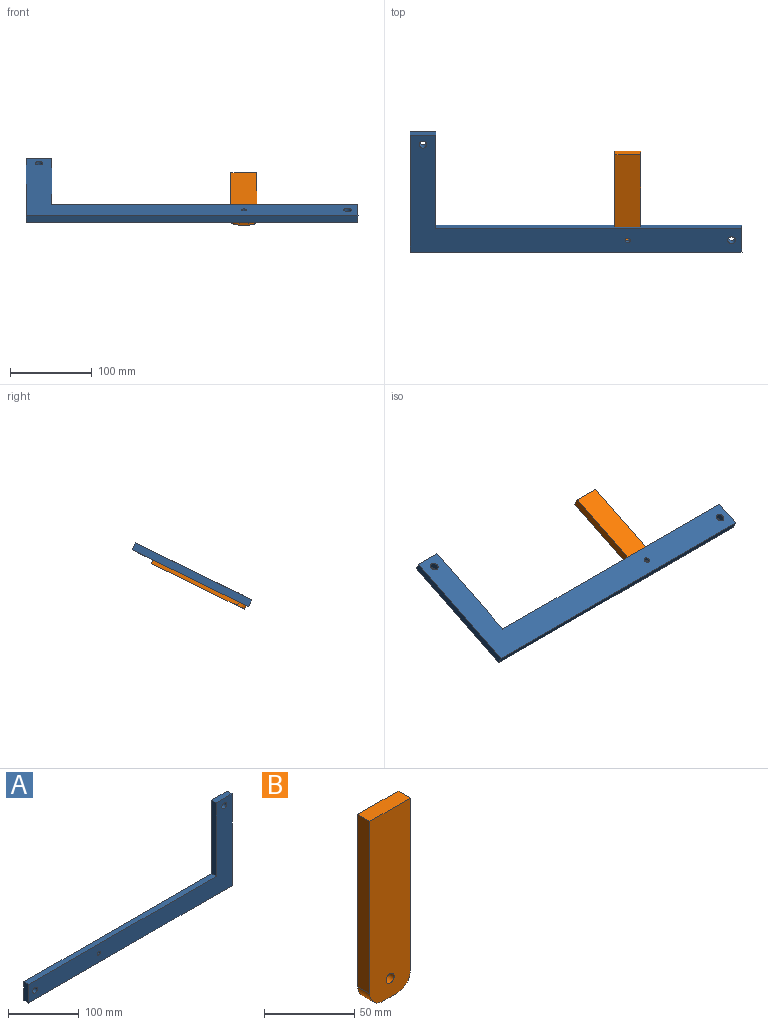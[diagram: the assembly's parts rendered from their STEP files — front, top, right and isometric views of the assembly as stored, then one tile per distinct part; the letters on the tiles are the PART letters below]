
ASSEMBLY  parts=2 mates=1
PART A: 11 faces, bbox 406.4x9.5x158.8 mm
  f0: plane 406.4x9.53mm, normal (0,0,-1), area 3871mm2, adj f1,f7,f9,f10
  f1: plane 158.75x9.53mm, normal (1,0,0), area 1512.1mm2, adj f0,f2,f9,f10
  f2: plane 31.75x9.53mm, normal (0,0,1), area 302.4mm2, adj f1,f3,f9,f10
  f3: plane 127x9.53mm, normal (-1,0,0), area 1209.7mm2, adj f2,f4,f9,f10
  f4: plane 374.65x9.53mm, normal (0,0,1), area 3568.5mm2, adj f3,f7,f9,f10
  f5: cylinder r=3.17mm len=9.53mm, axis (0,1,0), area 190mm2, adj f9,f10
  f6: cylinder r=4.76mm len=9.53mm, axis (0,1,0), area 285mm2, adj f9,f10
  f7: plane 31.75x9.53mm, normal (-1,0,0), area 302.4mm2, adj f0,f4,f9,f10
  f8: cylinder r=4.76mm len=9.53mm, axis (0,1,0), area 285mm2, adj f9,f10
  f9: plane 406.4x158.75mm, normal (0,-1,0), area 16761.3mm2, adj f0,f1,f2,f3,f4,f5,f6,f7
  f10: plane 406.4x158.75mm, normal (0,1,0), area 16761.3mm2, adj f0,f1,f2,f3,f4,f5,f6,f7
PART B: 9 faces, bbox 31.8x9.5x127 mm
  f0: plane 11.43x9.53mm, normal (0,0,-1), area 108.9mm2, adj f5,f6,f7,f8
  f1: plane 116.84x9.53mm, normal (1,0,0), area 1112.9mm2, adj f2,f5,f6,f7
  f2: plane 31.75x9.53mm, normal (0,0,1), area 302.4mm2, adj f1,f4,f5,f6
  f3: cylinder r=3.17mm len=9.53mm, axis (0,1,0), area 190mm2, adj f5,f6
  f4: plane 116.84x9.53mm, normal (-1,0,0), area 1112.9mm2, adj f2,f5,f6,f8
  f5: plane 127x31.75mm, normal (0,-1,0), area 3956.3mm2, adj f0,f1,f2,f3,f4,f7,f8
  f6: plane 127x31.75mm, normal (0,1,0), area 3956.3mm2, adj f0,f1,f2,f3,f4,f7,f8
  f7: cylinder r=10.16mm len=10.16mm, axis (0,-1,0), area 152mm2, adj f0,f1,f5,f6
  f8: cylinder r=10.16mm len=10.16mm, axis (0,1,0), area 152mm2, adj f0,f4,f5,f6
PLACE A rot(axis=(0,-0.53,-0.85),180deg) t=(-186.37,42.97,49.78)mm fixed
PLACE B rot(axis=(-1,0,0),64deg) t=(-122.87,94.89,59.2)mm
MATE fastened A.f5 <-> B.f3  axis (0,-0.44,0.9) through (-122.87,45.06,45.5)mm
